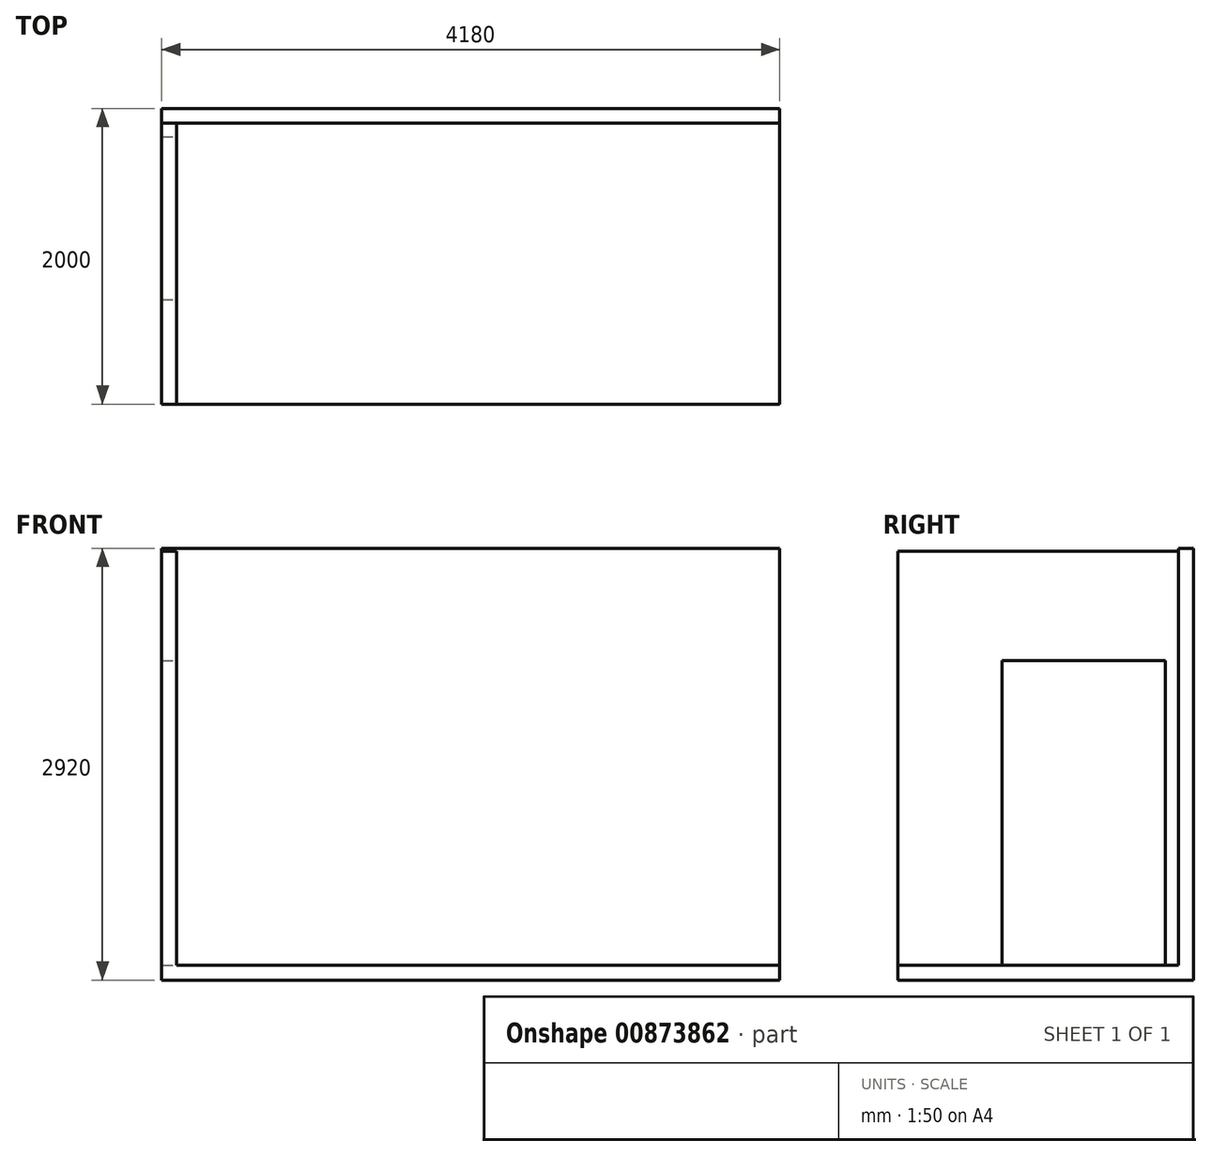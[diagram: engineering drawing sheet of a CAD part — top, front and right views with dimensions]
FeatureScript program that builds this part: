
annotation { "Feature Type Name" : "Feature", "Feature Type Description" : "" }
export const myFeature = defineFeature(function(context is Context, id is Id, definition is map)
    precondition{}
    {
        {
            var Q0;
            Q0=qCreatedBy(makeId("Top.planeOp"),FACE);
            var sketch = newSketch(context, id + "F0", { "sketchPlane" : qUnion([Q0])});
            skLineSegment(sketch, "E0.bottom", {"start": v(0, 0) * mm, "end": v(49.68, 0) * mm});
            skLineSegment(sketch, "E0.top", {"start": v(0, -40.5) * mm, "end": v(49.68, -40.5) * mm});
            skLineSegment(sketch, "E0.left", {"start": v(0, 0) * mm, "end": v(0, -40.5) * mm});
            skLineSegment(sketch, "E0.right", {"start": v(49.68, 0) * mm, "end": v(49.68, -40.5) * mm});
            skSolve(sketch);
        }
        {
            var Q0;
            Q0=makeQuery(id+"F0.imprint","IMPRINT",FACE,{"disambiguationData":[TD([[makeQuery(id+"F0.imprint","IMPRINT",EDGE,{"derivedFrom":sQuery(id+"F0.wireOp",EDGE,"E0.bottom")}),-1.0]])]});
            extrude(context, id + "F1", {"entities" : qUnion([Q0]), "depth" : 100 * mm, "offsetDistance" : 25.4 * mm});
        }
        {
            var Q0;
            Q0=makeQuery(id+"F1.opExtrude","SWEPT_FACE",FACE,{"disambiguationData":[OSD([sQuery(id+"F0.wireOp",EDGE,"E0.left")])]});
            extrude(context, id + "F2", {"entities" : qUnion([Q0]), "operationType" : NewBodyOperationType.ADD, "oppositeDirection" : true, "depth" : 4280 * mm, "offsetDistance" : 25 * mm});
        }
        {
            var Q0;
            {var subQ0=sQuery(id+"F0.wireOp",EDGE,"E0.bottom");Q0=makeQuery(id+"F2.boolean.opBoolean","MERGE",FACE,{"derivedFrom":[makeQuery(id+"F1.opExtrude","SWEPT_FACE",FACE,{"disambiguationData":[OSD([subQ0])]}),makeQuery(id+"F2.opExtrude","SWEPT_FACE",FACE,{"disambiguationData":[OSD([subQ0,sQuery(id+"F0.wireOp",EDGE,"E0.left")])]})]});}
            extrude(context, id + "F3", {"entities" : qUnion([Q0]), "operationType" : NewBodyOperationType.ADD, "oppositeDirection" : true, "depth" : 2000 * mm, "offsetDistance" : 25 * mm});
        }
        {
            var Q0;
            {var subQ0=sQuery(id+"F0.wireOp",EDGE,"E0.left");var subQ1=sQuery(id+"F0.wireOp",EDGE,"E0.bottom");Q0=makeQuery(id+"F3.boolean.opBoolean","MERGE",FACE,{"derivedFrom":[makeQuery(id+"F2.boolean.opBoolean","MERGE",FACE,{"derivedFrom":[makeQuery(id+"F1.opExtrude","CAP_FACE",FACE,{"disambiguationData":[OSD([subQ1,sQuery(id+"F0.wireOp",EDGE,"E0.top"),subQ0,sQuery(id+"F0.wireOp",EDGE,"E0.right")])],"isStart":false}),makeQuery(id+"F2.opExtrude","SWEPT_FACE",FACE,{"disambiguationData":[OSD([subQ0]),TDD([makeQuery(id+"F1.opExtrude","CAP_EDGE",EDGE,{"disambiguationData":[OSD([subQ0])],"isStart":false})])]})]}),makeQuery(id+"F3.opExtrude","SWEPT_FACE",FACE,{"disambiguationData":[OSD([subQ1,subQ0]),TDD([makeQuery(id+"F2.boolean.opBoolean","MERGE",EDGE,{"derivedFrom":[makeQuery(id+"F1.opExtrude","CAP_EDGE",EDGE,{"disambiguationData":[OSD([subQ1])],"isStart":false}),makeQuery(id+"F2.opExtrude","SWEPT_EDGE",EDGE,{"disambiguationData":[OSD([subQ1,subQ0]),TDD([makeQuery(id+"F1.opExtrude","CAP_VERTEX",VERTEX,{"disambiguationData":[OSD([subQ1,subQ0])],"isStart":false})])]})]})])]})]});}
            var sketch = newSketch(context, id + "F4", { "sketchPlane" : qUnion([Q0])});
            skLineSegment(sketch, "E1.0", {"start": v(0, -100) * mm, "end": v(4280, -100) * mm});
            skSolve(sketch);
        }
        {
            var Q0;
            {var subQ0=sQuery(id+"F4.wireOp",EDGE,"E1.0");Q0=makeQuery(id+"F4.imprint","IMPRINT",FACE,{"disambiguationData":[TD([[makeQuery(id+"F4.imprint","IMPRINT",EDGE,{"derivedFrom":subQ0}),-1.0]])]});}
            var sketch = newSketch(context, id + "F5", { "sketchPlane" : qUnion([Q0])});
            skLineSegment(sketch, "E2.0", {"start": v(100, 0) * mm, "end": v(100, -2000) * mm});
            skSolve(sketch);
        }
        {
            var Q0;
            {var subQ0=sQuery(id+"F4.wireOp",EDGE,"E1.0");Q0=makeQuery(id+"F4.imprint","IMPRINT",FACE,{"disambiguationData":[TD([[makeQuery(id+"F4.imprint","IMPRINT",EDGE,{"derivedFrom":subQ0}),1.0]])]});}
            extrude(context, id + "F6", {"entities" : qUnion([Q0]), "operationType" : NewBodyOperationType.ADD, "depth" : 2820 * mm, "offsetDistance" : 25 * mm});
        }
        {
            var Q0;
            {var subQ0=sQuery(id+"F5.wireOp",EDGE,"E2.0");var subQ7=sQuery(id+"F4.wireOp",EDGE,"E1.0");var subQ8=makeQuery(id+"F4.imprint","IMPRINT",EDGE,{"derivedFrom":subQ7});var subQ9=makeQuery(id+"F5.imprint","INTERSECT",VERTEX,{"derivedFrom":[subQ8,subQ0]});Q0=makeQuery(id+"F5.imprint","IMPRINT",FACE,{"disambiguationData":[TD([[makeQuery(id+"F5.imprint","IMPRINT",EDGE,{"disambiguationData":[TD([[subQ9,-1.0]])],"derivedFrom":subQ0}),-1.0]])]});}
            extrude(context, id + "F7", {"entities" : qUnion([Q0]), "operationType" : NewBodyOperationType.ADD, "depth" : 2800 * mm, "offsetDistance" : 25 * mm});
        }
        {
            var Q0;
            Q0=makeQuery(id+"F7.opExtrude","SWEPT_FACE",FACE,{"disambiguationData":[OSD([sQuery(id+"F5.wireOp",EDGE,"E2.0")])]});
            var sketch = newSketch(context, id + "F8", { "sketchPlane" : qUnion([Q0])});
            skLineSegment(sketch, "E3.bottom", {"start": v(-249.32, 100) * mm, "end": v(-1381.93, 100) * mm});
            skLineSegment(sketch, "E3.top", {"start": v(-249.32, 2309.35) * mm, "end": v(-1381.93, 2309.35) * mm});
            skLineSegment(sketch, "E3.left", {"start": v(-249.32, 100) * mm, "end": v(-249.32, 2309.35) * mm});
            skLineSegment(sketch, "E3.right", {"start": v(-1381.93, 100) * mm, "end": v(-1381.93, 2309.35) * mm});
            skSolve(sketch);
        }
        {
            var Q0;
            Q0=makeQuery(id+"F8.imprint","IMPRINT",FACE,{"disambiguationData":[TD([[makeQuery(id+"F8.imprint","IMPRINT",EDGE,{"derivedFrom":sQuery(id+"F8.wireOp",EDGE,"E3.bottom")}),-1.0]])]});
            extrude(context, id + "F9", {"entities" : qUnion([Q0]), "operationType" : NewBodyOperationType.REMOVE, "oppositeDirection" : true, "depth" : 100 * mm, "offsetDistance" : 25 * mm});
        }
        {
            var Q0;
            Q0=makeQuery(id+"F9.boolean.opBoolean","COPY",FACE,{"derivedFrom":makeQuery(id+"F9.opExtrude","SWEPT_FACE",FACE,{"disambiguationData":[OSD([sQuery(id+"F8.wireOp",EDGE,"E3.left")])]})});
            extrude(context, id + "F10", {"entities" : qUnion([Q0]), "operationType" : NewBodyOperationType.REMOVE, "oppositeDirection" : true, "depth" : 57.96 * mm, "offsetDistance" : 25 * mm});
        }
        {
            var Q0;
            Q0=makeQuery(id+"F9.boolean.opBoolean","COPY",FACE,{"derivedFrom":makeQuery(id+"F9.opExtrude","SWEPT_FACE",FACE,{"disambiguationData":[OSD([sQuery(id+"F8.wireOp",EDGE,"E3.right")])]})});
            extrude(context, id + "F11", {"entities" : qUnion([Q0]), "operationType" : NewBodyOperationType.ADD, "depth" : 87.98 * mm, "offsetDistance" : 25 * mm});
        }
        {
            var Q0;
            {var subQ0=sQuery(id+"F8.wireOp",EDGE,"E3.top");Q0=makeQuery(id+"F10.boolean.opBoolean","MERGE",FACE,{"derivedFrom":[makeQuery(id+"F9.boolean.opBoolean","COPY",FACE,{"derivedFrom":makeQuery(id+"F9.opExtrude","SWEPT_FACE",FACE,{"disambiguationData":[OSD([subQ0])]})}),makeQuery(id+"F10.opExtrude","SWEPT_FACE",FACE,{"disambiguationData":[OSD([subQ0,sQuery(id+"F8.wireOp",EDGE,"E3.left")])]})]});}
            extrude(context, id + "F12", {"entities" : qUnion([Q0]), "operationType" : NewBodyOperationType.ADD, "depth" : 149.94 * mm, "offsetDistance" : 25 * mm});
        }
        {
            var Q0;
            {var subQ0=sQuery(id+"F0.wireOp",EDGE,"E0.left");var subQ1=sQuery(id+"F0.wireOp",EDGE,"E0.bottom");var subQ2=makeQuery(id+"F1.opExtrude","CAP_VERTEX",VERTEX,{"disambiguationData":[OSD([subQ1,subQ0])],"isStart":false});var subQ3=makeQuery(id+"F3.boolean.opBoolean","MERGE",EDGE,{"derivedFrom":[makeQuery(id+"F2.opExtrude","CAP_EDGE",EDGE,{"disambiguationData":[OSD([subQ0]),TDD([makeQuery(id+"F1.opExtrude","CAP_EDGE",EDGE,{"disambiguationData":[OSD([subQ0])],"isStart":false})])],"isStart":false}),makeQuery(id+"F3.opExtrude","SWEPT_EDGE",EDGE,{"disambiguationData":[OSD([subQ1,subQ0]),TDD([makeQuery(id+"F2.opExtrude","CAP_VERTEX",VERTEX,{"disambiguationData":[OSD([subQ1,subQ0]),TDD([subQ2])],"isStart":false})])]})]});Q0=makeQuery(id+"F6.boolean.opBoolean","MERGE",FACE,{"derivedFrom":[makeQuery(id+"F3.boolean.opBoolean","MERGE",FACE,{"derivedFrom":[makeQuery(id+"F2.opExtrude","CAP_FACE",FACE,{"disambiguationData":[OSD([subQ0])],"isStart":false}),makeQuery(id+"F3.opExtrude","SWEPT_FACE",FACE,{"disambiguationData":[OSD([subQ1,subQ0]),TDD([makeQuery(id+"F2.opExtrude","CAP_EDGE",EDGE,{"disambiguationData":[OSD([subQ1,subQ0])],"isStart":false})])]})]}),makeQuery(id+"F6.opExtrude","SWEPT_FACE",FACE,{"disambiguationData":[OSD([subQ1,subQ0]),TDD([makeQuery(id+"F4.imprint","IMPRINT",EDGE,{"disambiguationData":[TD([[makeQuery(id+"F4.imprint","INTERSECT",VERTEX,{"derivedFrom":[subQ3,sQuery(id+"F4.wireOp",EDGE,"E1.0")]}),1.0]])],"derivedFrom":subQ3})])]})]});}
            extrude(context, id + "F13", {"entities" : qUnion([Q0]), "operationType" : NewBodyOperationType.REMOVE, "oppositeDirection" : true, "depth" : 100 * mm, "offsetDistance" : 25 * mm});
        }
    });
